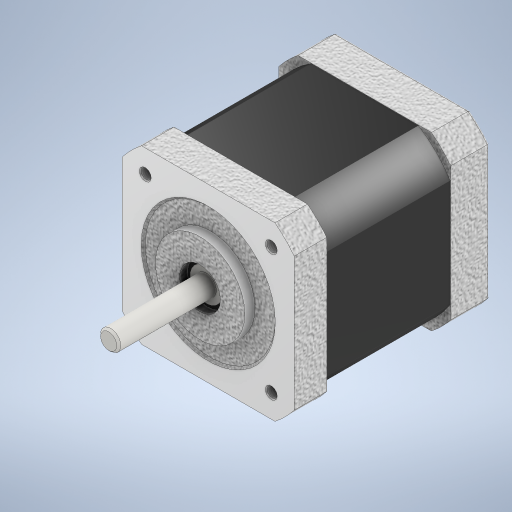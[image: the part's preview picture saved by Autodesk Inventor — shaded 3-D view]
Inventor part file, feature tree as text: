
AUTODESK INVENTOR PART (.ipt)
format: ipt  version: 2024 (Build 280153000, 153)  size: 581,120 bytes
history: native  units: mm
features: extrude x13, projected_geometry x6, chamfer x4, fillet x3, hole x2, plane x2, pattern_circular x2
ambient origin geometry x8: Origin, YZ Plane, XZ Plane, XY Plane, X Axis, Y Axis, Z Axis, Center Point
bodies: Solid1 (feature_tree)
feature tree (32):
  extrude  "Extrusion1"  Depth=42.3mm
  extrude  "Extrusion2"  Depth=42.3mm
  hole  "Hole1"  [1 undecoded]
  plane  "Work Plane1"
  extrude  "Extrusion3"  Depth=31.0mm
  extrude  "Extrusion5"  Depth=49.9mm
  chamfer  "Chamfer1"  Distance=22.0mm
  hole  "Hole2"  [1 undecoded]
  plane  "Work Plane2"
  extrude  "Extrusion6"  Depth=2.0mm TaperAngle=0.0deg
  chamfer  "Chamfer2"  [1 undecoded]
  extrude  "Extrusion7"  Depth=9.5mm TaperAngle=0.0deg
  extrude  "Extrusion8"  Depth=49.85mm
  extrude  "Extrusion9"  Depth=0.1mm
  extrude  "Extrusion10"  Depth=10.0mm TaperAngle=0.0deg
  extrude  "Extrusion11"  Depth=0.25mm TaperAngle=45.0deg
  chamfer  "Chamfer3"  Distance=5.0mm
  extrude  "Extrusion13"  Depth=8.0mm
  pattern_circular  "Circular Pattern1"  [2 undecoded]
  fillet  "Fillet2"  Radius=4.5mm
  fillet  "Fillet3"  Radius=0.5mm
  extrude  "Extrusion12"  Depth=22.298mm TaperAngle=0.0deg
  fillet  "Fillet1"  Radius=0.5mm
  pattern_circular  "Circular Pattern2"  [2 undecoded]
  extrude  "Extrusion14"  Depth=3.0mm TaperAngle=0.0deg
  chamfer  "Chamfer4"  Distance=8.0mm
  projected_geometry  "Projected Loop1"
  projected_geometry  "Projected Loop2"
  projected_geometry  "Projected Loop3"
  projected_geometry  "Projected Loop5"
  projected_geometry  "Projected Loop6"
  projected_geometry  "Projected Loop7"
note: 7 required parameter values undecoded (feature->parameter linkage not recoverable at this tier; creation-order binding heuristic only, values carry confidence <= 0.55)
